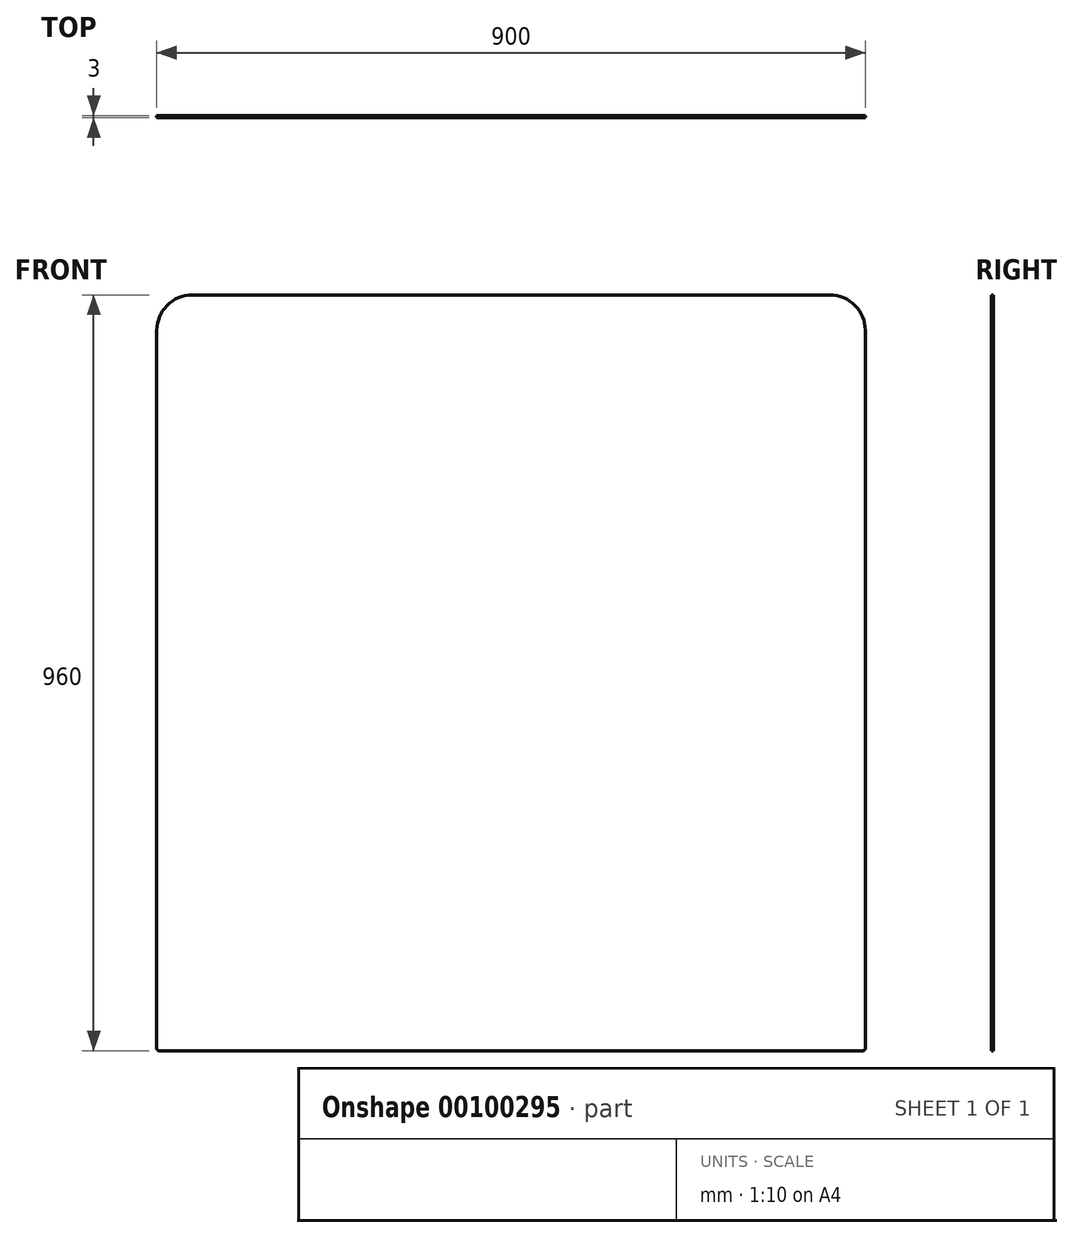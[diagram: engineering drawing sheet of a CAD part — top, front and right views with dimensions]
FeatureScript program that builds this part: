
annotation { "Feature Type Name" : "Feature", "Feature Type Description" : "" }
export const myFeature = defineFeature(function(context is Context, id is Id, definition is map)
    precondition{}
    {
        {
            var Q0;
            Q0=qCreatedBy(makeId("Front.planeOp"),FACE);
            var sketch = newSketch(context, id + "F0", { "sketchPlane" : qUnion([Q0])});
            skLineSegment(sketch, "E0", {"start": v(0, 960) * mm, "end": v(0, 0) * mm});
            skLineSegment(sketch, "E1", {"start": v(0, 0) * mm, "end": v(900, 0) * mm});
            skLineSegment(sketch, "E2", {"start": v(900, 0) * mm, "end": v(900, 960) * mm});
            skLineSegment(sketch, "E3", {"start": v(900, 960) * mm, "end": v(0, 960) * mm});
            skSolve(sketch);
        }
        {
            var Q0;
            Q0=qSketchRegion(id+"F0",true);
            extrude(context, id + "F1", {"entities" : qUnion([Q0]), "depth" : 3 * mm});
        }
        {
            var Q0;
            Q0=makeQuery(id+"F1.opExtrude","SWEPT_EDGE",EDGE,{"disambiguationData":[OSD([sQuery(id+"F0.wireOp",EDGE,"E2"),sQuery(id+"F0.wireOp",EDGE,"E3")])]});
            var Q1;
            Q1=makeQuery(id+"F1.opExtrude","SWEPT_EDGE",EDGE,{"disambiguationData":[OSD([sQuery(id+"F0.wireOp",EDGE,"E0"),sQuery(id+"F0.wireOp",EDGE,"E3")])]});
            fillet(context, id + "F2", {"entities" : qUnion([Q0, Q1]), "radius" : 45 * mm, "tangentPropagation" : true, "allowEdgeOverflow" : false});
        }
        {
            var Q0;
            Q0=makeQuery(id+"F1.opExtrude","SWEPT_EDGE",EDGE,{"disambiguationData":[OSD([sQuery(id+"F0.wireOp",EDGE,"E1"),sQuery(id+"F0.wireOp",EDGE,"E2")])]});
            var Q1;
            Q1=makeQuery(id+"F1.opExtrude","SWEPT_EDGE",EDGE,{"disambiguationData":[OSD([sQuery(id+"F0.wireOp",EDGE,"E0"),sQuery(id+"F0.wireOp",EDGE,"E1")])]});
            fillet(context, id + "F3", {"entities" : qUnion([Q0, Q1]), "radius" : 3 * mm, "tangentPropagation" : true, "allowEdgeOverflow" : false});
        }
    });
